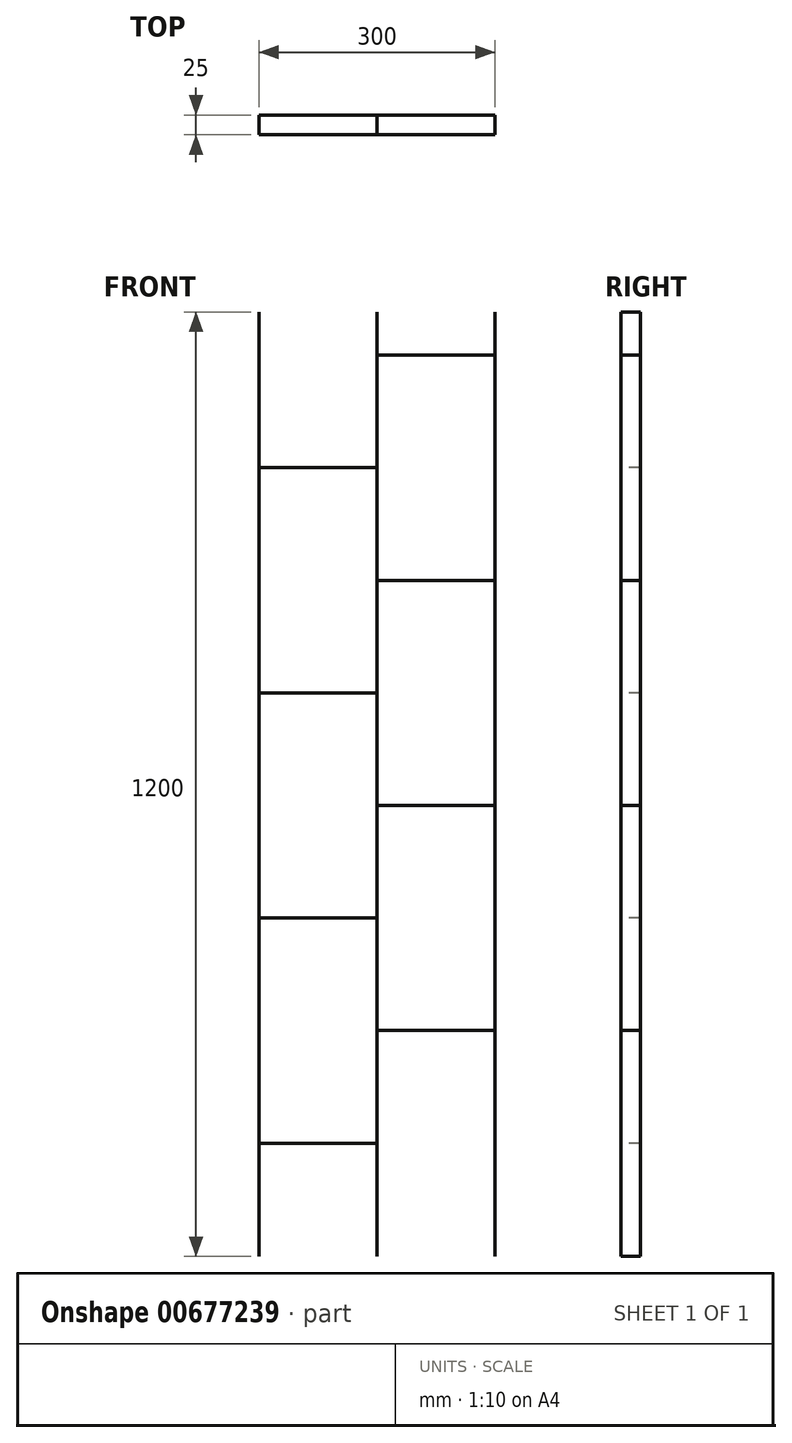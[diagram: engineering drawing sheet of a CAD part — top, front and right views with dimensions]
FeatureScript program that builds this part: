
annotation { "Feature Type Name" : "Feature", "Feature Type Description" : "" }
export const myFeature = defineFeature(function(context is Context, id is Id, definition is map)
    precondition{}
    {
        {
            var Q0;
            Q0=qCreatedBy(makeId("Front.planeOp"),FACE);
            var sketch = newSketch(context, id + "F0", { "sketchPlane" : qUnion([Q0])});
            skLineSegment(sketch, "E0.top", {"start": v(-250, -623.73) * mm, "end": v(250, -623.73) * mm});
            skLineSegment(sketch, "E0.left", {"start": v(-250, 576.27) * mm, "end": v(-250, -623.73) * mm});
            skLineSegment(sketch, "E0.right", {"start": v(250, 576.27) * mm, "end": v(250, -623.73) * mm});
            skLineSegment(sketch, "E1", {"start": v(-150, 576.27) * mm, "end": v(-150, -623.73) * mm});
            skLineSegment(sketch, "E2", {"start": v(0, 576.27) * mm, "end": v(0, -623.73) * mm});
            skLineSegment(sketch, "E3", {"start": v(150, 576.27) * mm, "end": v(150, -623.73) * mm});
            skLineSegment(sketch, "E4", {"start": v(150, 521.27) * mm, "end": v(0, 521.27) * mm});
            skLineSegment(sketch, "E5", {"start": v(150, 235.27) * mm, "end": v(0, 235.27) * mm});
            skLineSegment(sketch, "E6", {"start": v(150, -50.73) * mm, "end": v(0, -50.73) * mm});
            skLineSegment(sketch, "E7", {"start": v(150, -336.73) * mm, "end": v(0, -336.73) * mm});
            skLineSegment(sketch, "E8", {"start": v(-150, -479.73) * mm, "end": v(0, -479.73) * mm});
            skLineSegment(sketch, "E9", {"start": v(-150, -193.73) * mm, "end": v(0, -193.73) * mm});
            skLineSegment(sketch, "E10", {"start": v(-150, 92.27) * mm, "end": v(0, 92.27) * mm});
            skLineSegment(sketch, "E11", {"start": v(-150, 378.27) * mm, "end": v(0, 378.27) * mm});
            skLineSegment(sketch, "E12", {"start": v(-250, 576.27) * mm, "end": v(250, 576.27) * mm});
            skSolve(sketch);
        }
        {
            var Q0;
            Q0=sQuery(id+"F0.wireOp",EDGE,"E4");
            var Q1;
            Q1=sQuery(id+"F0.wireOp",EDGE,"E11");
            var Q2;
            Q2=sQuery(id+"F0.wireOp",EDGE,"E5");
            var Q3;
            Q3=sQuery(id+"F0.wireOp",EDGE,"E10");
            var Q4;
            Q4=sQuery(id+"F0.wireOp",EDGE,"E6");
            var Q5;
            Q5=sQuery(id+"F0.wireOp",EDGE,"E9");
            var Q6;
            Q6=sQuery(id+"F0.wireOp",EDGE,"E7");
            var Q7;
            Q7=sQuery(id+"F0.wireOp",EDGE,"E8");
            extrude(context, id + "F1", {"bodyType" : ToolBodyType.SURFACE, "surfaceEntities" : qUnion([Q0, Q1, Q2, Q3, Q4, Q5, Q6, Q7]), "depth" : 25 * mm, "offsetDistance" : 25 * mm});
        }
        {
            var Q0;
            Q0=sQuery(id+"F0.wireOp",EDGE,"E1");
            var Q1;
            Q1=sQuery(id+"F0.wireOp",EDGE,"E2");
            var Q2;
            Q2=sQuery(id+"F0.wireOp",EDGE,"E3");
            extrude(context, id + "F2", {"bodyType" : ToolBodyType.SURFACE, "surfaceEntities" : qUnion([Q0, Q1, Q2]), "depth" : 25 * mm, "offsetDistance" : 25 * mm});
        }
    });
